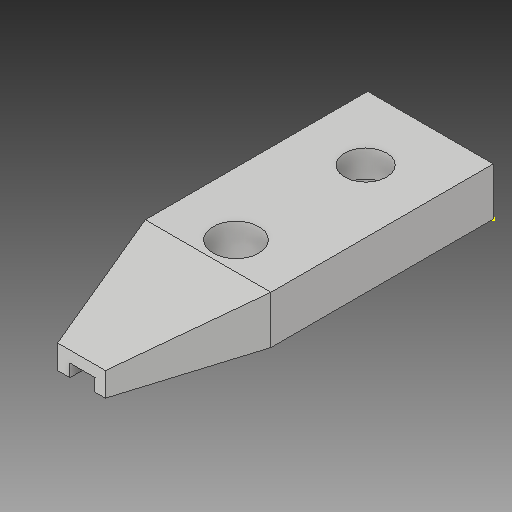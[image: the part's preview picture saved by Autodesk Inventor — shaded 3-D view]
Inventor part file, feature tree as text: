
AUTODESK INVENTOR PART (.ipt)
format: ipt  version: 2019 (Build 230136000, 136)  size: 128,512 bytes
history: native  units: mm
features: sketch x6, extrude x4, hole x1
ambient origin geometry x8: Origin, YZ Plane, XZ Plane, XY Plane, X Axis, Y Axis, Z Axis, Center Point
bodies: Solid1 (feature_tree)
feature tree (11):
  extrude  "Extrusion1"  Depth=22.3mm
  hole  "Hole1"  [1 undecoded]
  extrude  "Extrusion2"  Depth=10.0mm TaperAngle=0.0deg
  extrude  "Extrusion3"  Depth=2.0mm
  sketch  "Sketch5"  dims[d18=2.5mm d19=2.0mm]
  extrude  "Extrusion4"  [1 undecoded]
  sketch  "Sketch1"  dims[d2=4.8mm d3=0.0mm d4=22.3mm]
  sketch  "Sketch2"  dims[d5=4.8mm]
  sketch  "Sketch3"  dims[d6=4.2mm d7=6.0mm d8=8.4mm d9=2.0mm d10=90.0deg d11=8.0mm d12=20.594885mm d13=4.6mm]
  sketch  "Sketch4"  dims[d14=4.8mm d15=0.0mm d16=10.0mm d17=0.0mm]
  sketch  "Sketch6"  dims[d20=1.27mm d21=0.0mm]
note: 2 required parameter values undecoded (feature->parameter linkage not recoverable at this tier; creation-order binding heuristic only, values carry confidence <= 0.55)
